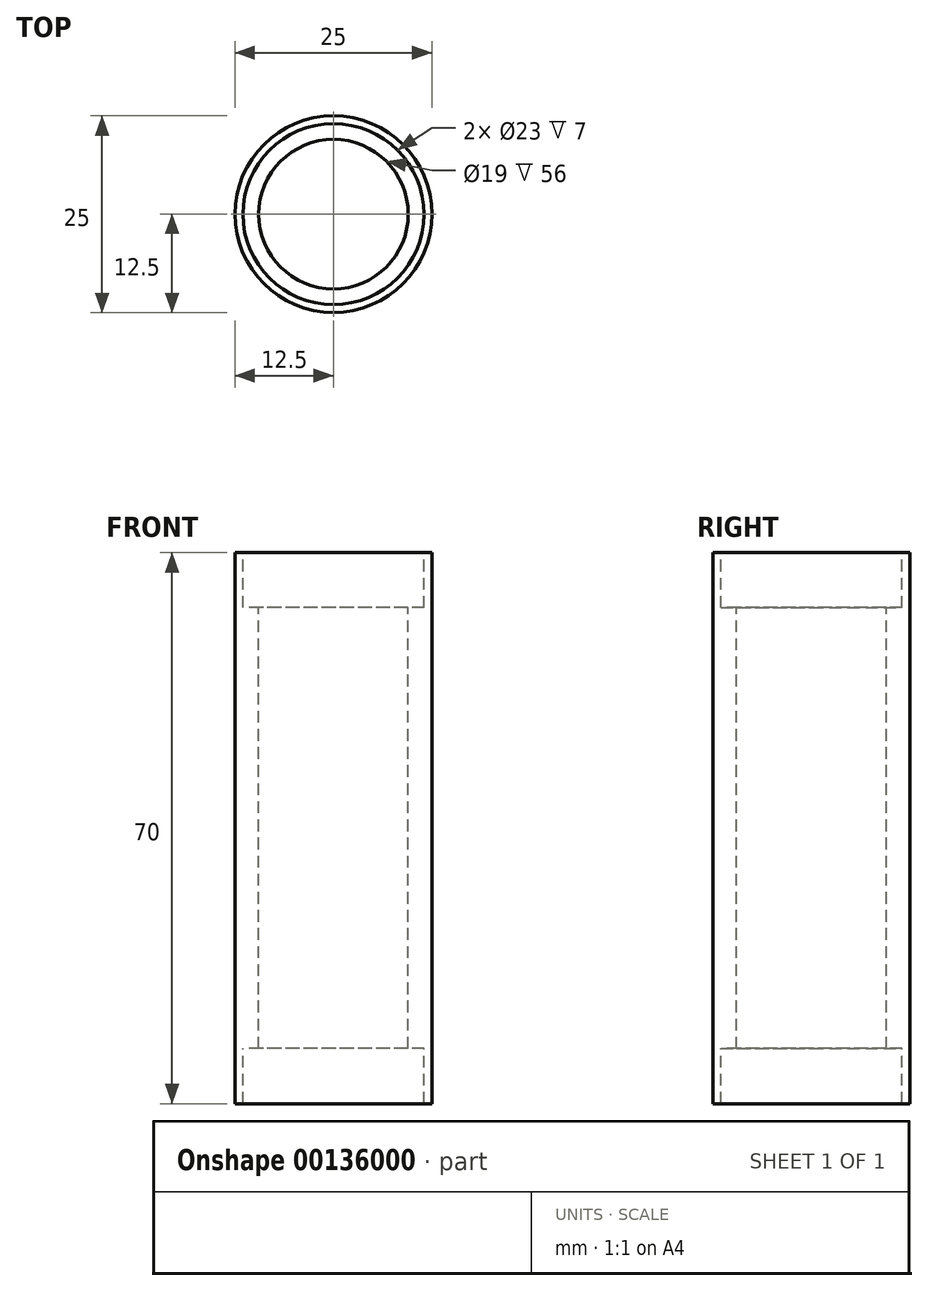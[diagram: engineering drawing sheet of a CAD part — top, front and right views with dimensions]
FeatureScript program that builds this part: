
annotation { "Feature Type Name" : "Feature", "Feature Type Description" : "" }
export const myFeature = defineFeature(function(context is Context, id is Id, definition is map)
    precondition{}
    {
        {
            var Q0;
            Q0=qCreatedBy(makeId("Front.planeOp"),FACE);
            var sketch = newSketch(context, id + "F1", { "sketchPlane" : qUnion([Q0])});
            skLineSegment(sketch, "E0", {"start": v(16.75, 35) * mm, "end": v(16.75, 28) * mm});
            skLineSegment(sketch, "E1", {"start": v(16.75, 28) * mm, "end": v(14.75, 28) * mm});
            skLineSegment(sketch, "E2", {"start": v(-40.59, 0) * mm, "end": v(40.41, 0) * mm, "construction": true});
            skLineSegment(sketch, "E3.MirrorCS", {"start": v(16.75, -28) * mm, "end": v(14.75, -28) * mm});
            skLineSegment(sketch, "E4.MirrorCS", {"start": v(16.75, -35) * mm, "end": v(16.75, -28) * mm});
            skLineSegment(sketch, "E5", {"start": v(14.75, 28) * mm, "end": v(14.75, -28) * mm});
            skLineSegment(sketch, "E6", {"start": v(16.75, 35) * mm, "end": v(17.75, 35) * mm});
            skLineSegment(sketch, "E7", {"start": v(17.75, 35) * mm, "end": v(17.75, -35) * mm});
            skLineSegment(sketch, "E8", {"start": v(16.75, -35) * mm, "end": v(17.75, -35) * mm});
            skLineSegment(sketch, "E9", {"start": v(0, 61.9) * mm, "end": v(5.25, 61.9) * mm});
            skLineSegment(sketch, "E10", {"start": v(5.25, 61.9) * mm, "end": v(5.25, -67.08) * mm, "construction": true});
            skSolve(sketch);
        }
        {
            var Q0;
            Q0=makeQuery(id+"F1.imprint","IMPRINT",FACE,{"disambiguationData":[TD([[makeQuery(id+"F1.imprint","IMPRINT",EDGE,{"derivedFrom":sQuery(id+"F1.wireOp",EDGE,"E0")}),1.0]])]});
            var Q1;
            Q1=sQuery(id+"F1.wireOp",EDGE,"E10");
            revolve(context, id + "F0", {"entities" : qUnion([Q0]), "axis" : qUnion([Q1]), "revolveType" : RevolveType.FULL});
        }
    });
